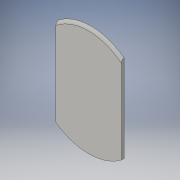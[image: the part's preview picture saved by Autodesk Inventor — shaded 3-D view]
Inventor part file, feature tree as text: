
AUTODESK INVENTOR PART (.ipt)
format: ipt  version: 2016 (Build 200138000, 138)  size: 96,768 bytes
history: native  units: in
note: dims shown in document units (in); Inventor stores cm internally (conversion verified against a paired STEP export)
features: extrude x1, fillet x1, sketch x1
ambient origin geometry x8: Origin, YZ Plane, XZ Plane, XY Plane, X Axis, Y Axis, Z Axis, Center Point
bodies: Solid1 (feature_tree)
feature tree (3):
  extrude  "Extrusion1"  Depth=0.125in
  fillet  "Fillet1"  [1 undecoded]
  sketch  "Sketch1"  dims[d2=0.125in d3=0.0in d4=0.125in]
note: 1 required parameter value undecoded (feature->parameter linkage not recoverable at this tier; creation-order binding heuristic only, values carry confidence <= 0.55)
